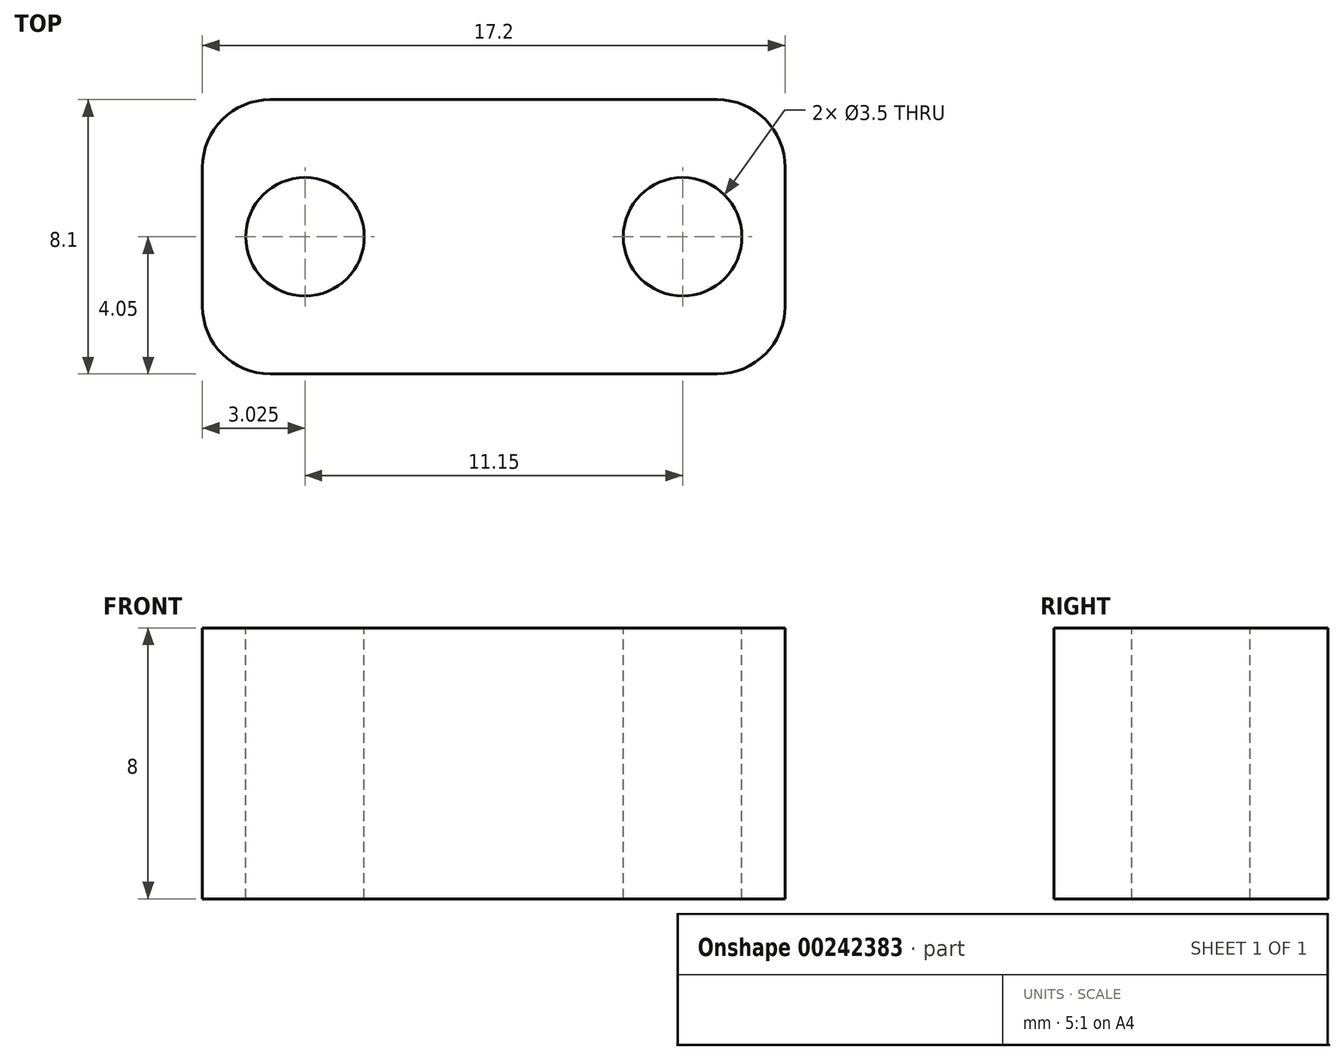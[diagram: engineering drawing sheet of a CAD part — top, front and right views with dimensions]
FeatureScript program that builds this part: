
annotation { "Feature Type Name" : "Feature", "Feature Type Description" : "" }
export const myFeature = defineFeature(function(context is Context, id is Id, definition is map)
    precondition{}
    {
        {
            var Q0;
            Q0=qCreatedBy(makeId("Front.planeOp"),FACE);
            var sketch = newSketch(context, id + "F0", { "sketchPlane" : qUnion([Q0])});
            skLineSegment(sketch, "E0", {"start": v(-8.6, 0) * mm, "end": v(-8.6, 8) * mm});
            skLineSegment(sketch, "E1", {"start": v(-8.6, 8) * mm, "end": v(8.6, 8) * mm});
            skLineSegment(sketch, "E2", {"start": v(8.6, 8) * mm, "end": v(8.6, 0) * mm});
            skLineSegment(sketch, "E3", {"start": v(8.6, 0) * mm, "end": v(-8.6, 0) * mm});
            skSolve(sketch);
        }
        {
            var Q0;
            Q0=qSketchRegion(id+"F0",true);
            extrude(context, id + "F1", {"entities" : qUnion([Q0]), "depth" : 8.1 * mm});
        }
        {
            var Q0;
            Q0=makeQuery(id+"F1.opExtrude","SWEPT_FACE",FACE,{"disambiguationData":[OSD([sQuery(id+"F0.wireOp",EDGE,"E1")])]});
            var sketch = newSketch(context, id + "F2", { "sketchPlane" : qUnion([Q0])});
            skLineSegment(sketch, "E4", {"start": v(-12.2, -4.05) * mm, "end": v(13.93, -4.05) * mm, "construction": true});
            skPoint(sketch, "E4.startSnap0", {"position": v(-8.6, -4.05) * mm});
            skPoint(sketch, "E4.endSnap0", {"position": v(8.6, -4.05) * mm});
            skCircle(sketch, "E5", {"center": v(-5.58, -4.05) * mm, "radius": 1.75 * mm});
            skCircle(sketch, "E6", {"center": v(5.58, -4.05) * mm, "radius": 1.75 * mm});
            skSolve(sketch);
        }
        {
            var Q0;
            Q0=qSketchRegion(id+"F2",true);
            extrude(context, id + "F3", {"entities" : qUnion([Q0]), "operationType" : NewBodyOperationType.REMOVE, "endBound" : BoundingType.THROUGH_ALL, "oppositeDirection" : true, "depth" : 25 * mm});
        }
        {
            var Q0;
            Q0=makeQuery(id+"F1.opExtrude","CAP_EDGE",EDGE,{"disambiguationData":[OSD([sQuery(id+"F0.wireOp",EDGE,"E0")])],"isStart":false});
            var Q1;
            Q1=makeQuery(id+"F1.opExtrude","CAP_EDGE",EDGE,{"disambiguationData":[OSD([sQuery(id+"F0.wireOp",EDGE,"E2")])],"isStart":false});
            var Q2;
            Q2=makeQuery(id+"F1.opExtrude","CAP_EDGE",EDGE,{"disambiguationData":[OSD([sQuery(id+"F0.wireOp",EDGE,"E2")])],"isStart":true});
            var Q3;
            Q3=makeQuery(id+"F1.opExtrude","CAP_EDGE",EDGE,{"disambiguationData":[OSD([sQuery(id+"F0.wireOp",EDGE,"E0")])],"isStart":true});
            fillet(context, id + "F4", {"entities" : qUnion([Q0, Q1, Q2, Q3]), "radius" : 2 * mm, "tangentPropagation" : true, "allowEdgeOverflow" : false});
        }
    });
